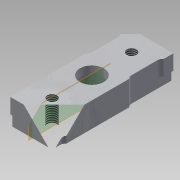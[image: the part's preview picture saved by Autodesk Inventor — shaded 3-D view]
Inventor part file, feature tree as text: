
AUTODESK INVENTOR PART (.ipt)
format: ipt  version: 2014 (Build 180170000, 170)  size: 213,504 bytes
history: native  units: mm
features: extrude x7, sketch x6, reference x4, thread x2, plane x1, mirror x1
ambient origin geometry x8: Origin, YZ Plane, XZ Plane, XY Plane, X Axis, Y Axis, Z Axis, Center Point
bodies: Solid1 (feature_tree)
feature tree (21):
  extrude  "Extrusion1"  Depth=15.0mm
  extrude  "Extrusion2"  Depth=4.0mm TaperAngle=0.0deg
  extrude  "Extrusion3"  Depth=2.4mm
  sketch  "Sketch6"  dims[d6=2.4mm d7=2.4mm]
  sketch  "Sketch7"  dims[d8=5.0mm d9=5.0mm]
  extrude  "Extrusion8"  Depth=5.0mm
  extrude  "Extrusion9"  Depth=0.5mm
  plane  "Work Plane1"
  mirror  "Mirror1"
  extrude  "Extrusion10"  Depth=3.0mm
  extrude  "Extrusion11"  Depth=4.0mm
  thread  "Thread1"  [1 undecoded]
  thread  "Thread2"  [1 undecoded]
  reference  "Reference1"
  sketch  "Sketch2"  dims[d0=5.5mm d1=15.0mm]
  reference  "Reference2"
  sketch  "Sketch3"  dims[d2=2.0mm d3=0.0mm d4=4.0mm d5=0.0mm]
  reference  "Reference3"
  reference  "Reference4"
  sketch  "Sketch8"  dims[d10=10.0mm d11=0.0mm d16=0.5mm d17=0.5mm]
  sketch  "Sketch9"  dims[d21=4.0mm d23=3.0mm d25=4.0mm d29=3.0mm d30=2.0mm d33=100.0mm d34=0.0mm d35=2.2mm d36=0.0mm d37=-5.5mm d38=10.0mm d39=3.5mm d40=0.5mm d41=1.5mm d42=0.2mm d43=0.0mm d44=6.0mm d45=100.0mm d46=0.0mm d47=10.0mm d48=0.0mm d49=10.0mm d50=0.0mm d51=0.5mm]
note: 2 required parameter values undecoded (feature->parameter linkage not recoverable at this tier; creation-order binding heuristic only, values carry confidence <= 0.55)
